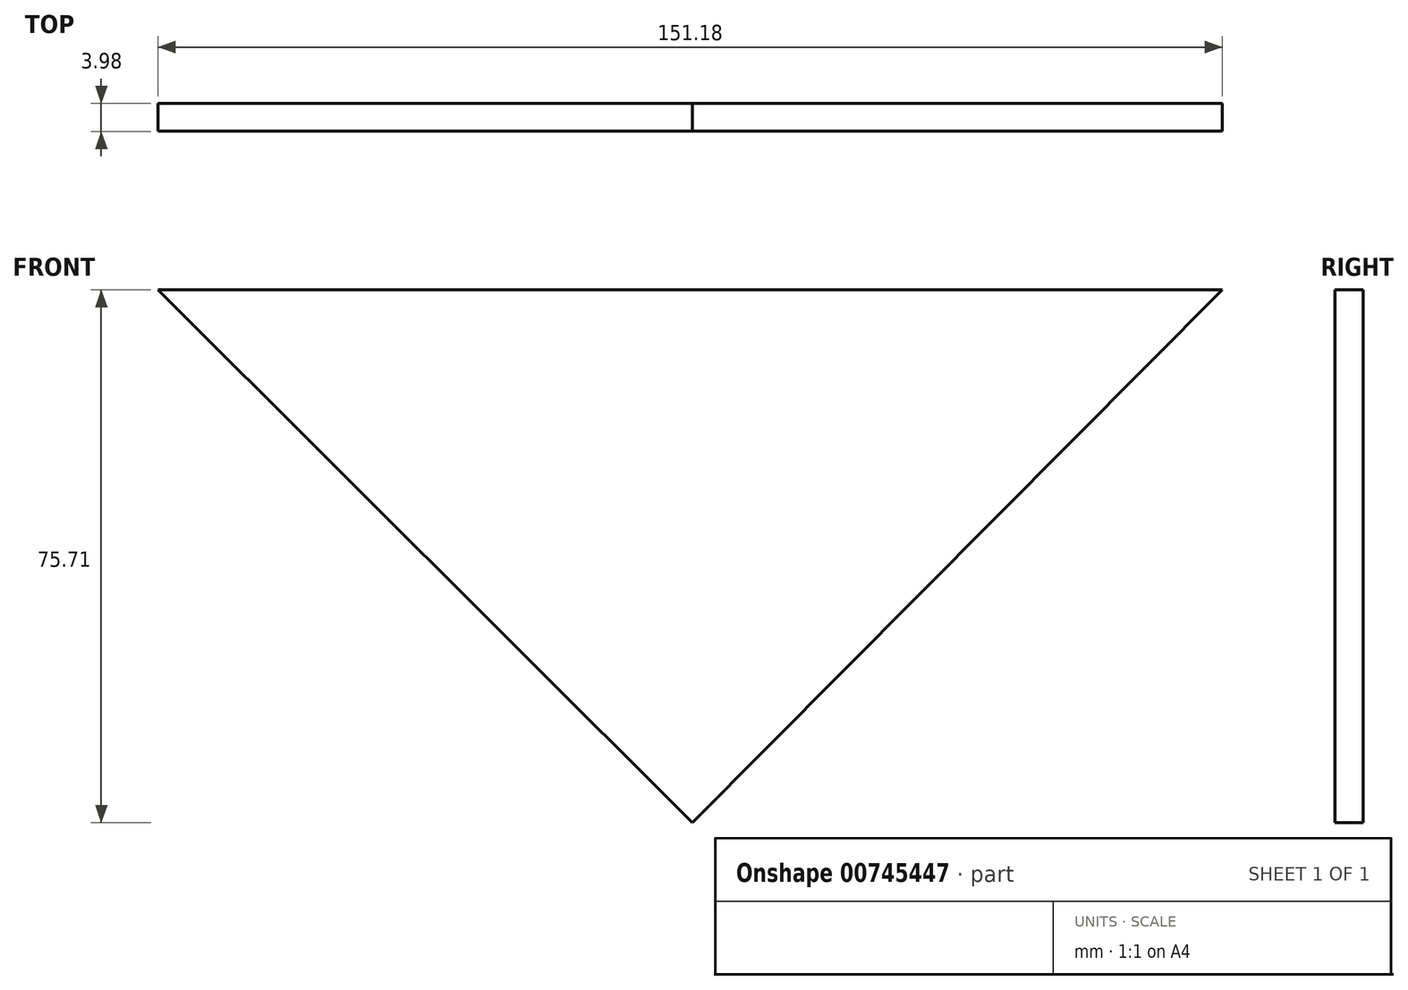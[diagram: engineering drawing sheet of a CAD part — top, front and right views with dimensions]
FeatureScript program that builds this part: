
annotation { "Feature Type Name" : "Feature", "Feature Type Description" : "" }
export const myFeature = defineFeature(function(context is Context, id is Id, definition is map)
    precondition{}
    {
        {
            var Q0;
            Q0=qCreatedBy(makeId("Front.planeOp"),FACE);
            var sketch = newSketch(context, id + "F0", { "sketchPlane" : qUnion([Q0])});
            skLineSegment(sketch, "E0", {"start": v(0, 0) * mm, "end": v(75.24, 0) * mm});
            skLineSegment(sketch, "E1", {"start": v(0, 0) * mm, "end": v(-75.94, 0) * mm});
            skLineSegment(sketch, "E2", {"start": v(-75.94, 0) * mm, "end": v(0, -75.71) * mm});
            skLineSegment(sketch, "E3", {"start": v(75.24, 0) * mm, "end": v(0, -75.71) * mm});
            skSolve(sketch);
        }
        {
            var Q0;
            Q0=sQuery(id+"F0.wireOp",EDGE,"E1");
            extrude(context, id + "F1", {"bodyType" : ToolBodyType.SURFACE, "surfaceEntities" : qUnion([Q0]), "depth" : 3.98 * mm, "offsetDistance" : 25.4 * mm});
        }
        {
            var Q0;
            Q0=sQuery(id+"F0.wireOp",EDGE,"E0");
            extrude(context, id + "F2", {"bodyType" : ToolBodyType.SURFACE, "surfaceEntities" : qUnion([Q0]), "depth" : 3.98 * mm, "offsetDistance" : 25.4 * mm});
        }
        {
            var Q0;
            Q0=sQuery(id+"F0.wireOp",EDGE,"E2");
            extrude(context, id + "F3", {"bodyType" : ToolBodyType.SURFACE, "surfaceEntities" : qUnion([Q0]), "depth" : 3.98 * mm, "offsetDistance" : 25.4 * mm});
        }
        {
            var Q0;
            Q0=sQuery(id+"F0.wireOp",EDGE,"E3");
            extrude(context, id + "F4", {"bodyType" : ToolBodyType.SURFACE, "surfaceEntities" : qUnion([Q0]), "depth" : 3.98 * mm, "offsetDistance" : 25.4 * mm});
        }
    });
